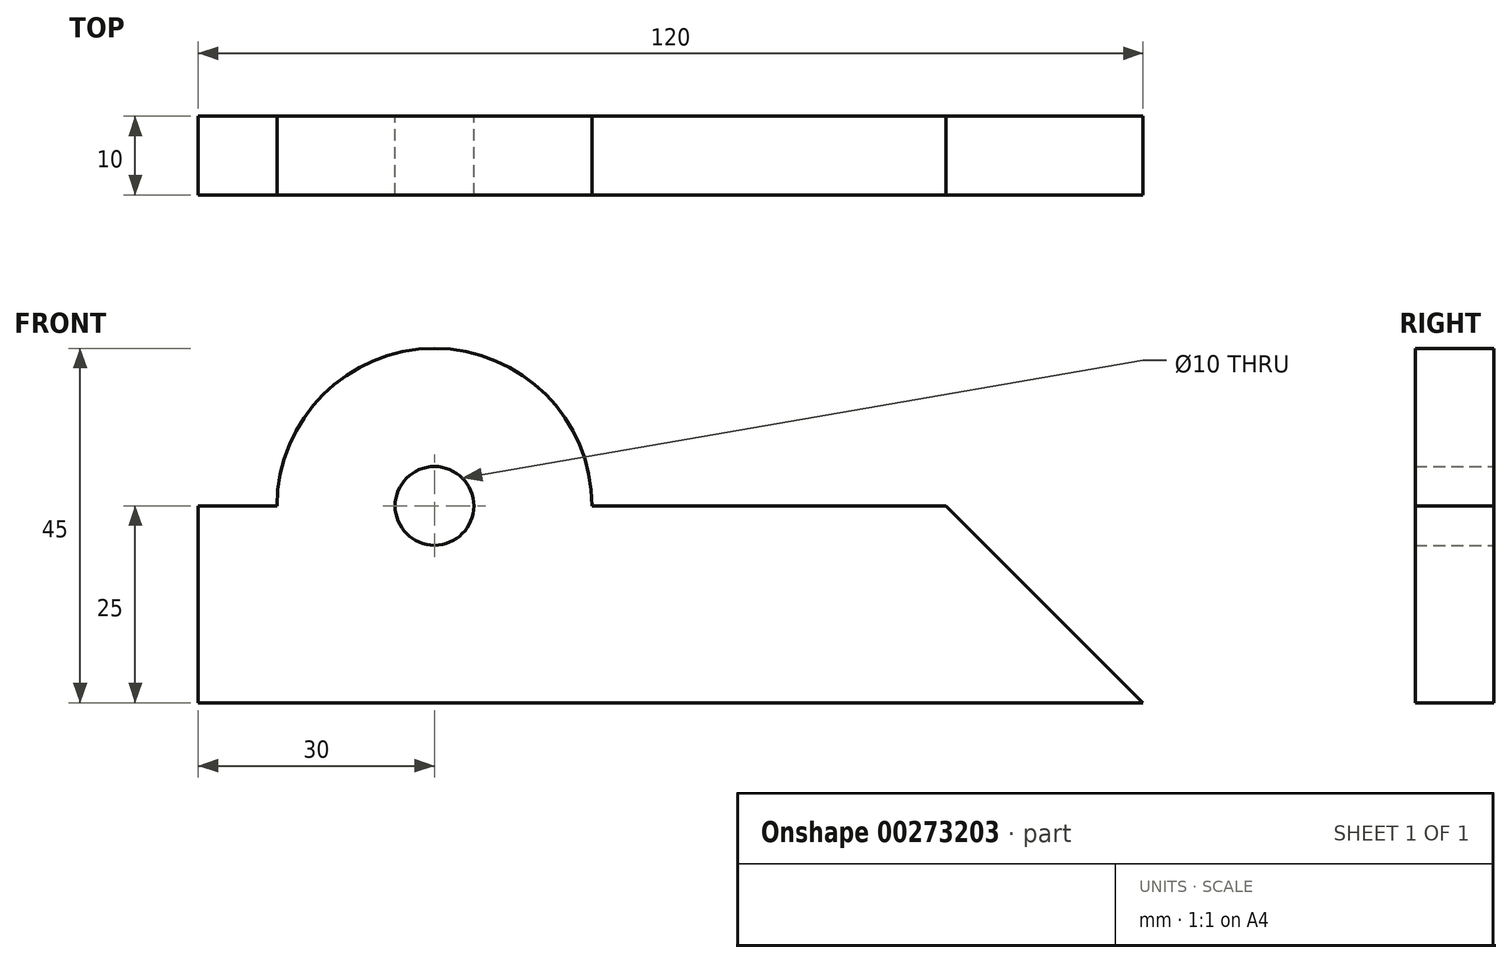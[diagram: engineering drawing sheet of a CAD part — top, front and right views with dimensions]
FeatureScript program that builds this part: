
annotation { "Feature Type Name" : "Feature", "Feature Type Description" : "" }
export const myFeature = defineFeature(function(context is Context, id is Id, definition is map)
    precondition{}
    {
        {
            var Q0;
            Q0=qCreatedBy(makeId("Front.planeOp"),FACE);
            var sketch = newSketch(context, id + "F0", { "sketchPlane" : qUnion([Q0])});
            skLineSegment(sketch, "E0", {"start": v(0, 0) * mm, "end": v(120, 0) * mm});
            skLineSegment(sketch, "E1", {"start": v(120, 0) * mm, "end": v(95, 25) * mm});
            skLineSegment(sketch, "E2", {"start": v(95, 25) * mm, "end": v(50, 25) * mm});
            skLineSegment(sketch, "E3", {"start": v(0, 0) * mm, "end": v(0, 25) * mm});
            skLineSegment(sketch, "E4", {"start": v(0, 25) * mm, "end": v(10, 25) * mm});
            skArc(sketch, "E5", {"start": v(50, 25) * mm, "mid": v(30, 45) * mm, "end": v(10, 25) * mm});
            skCircle(sketch, "E6", {"center": v(30, 25) * mm, "radius": 5 * mm});
            skSolve(sketch);
        }
        {
            var Q0;
            Q0 = qSketchRegion(id + "F0", true);
            extrude(context, id + "F1", {"entities" : qUnion([Q0]), "depth" : 10 * mm});
        }
    });
